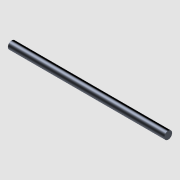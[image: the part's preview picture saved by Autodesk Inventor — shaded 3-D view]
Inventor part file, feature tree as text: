
AUTODESK INVENTOR PART (.ipt)
format: ipt  version: 2021 (Build 250183000, 183)  size: 96,768 bytes
history: native  units: in
note: dims shown in document units (in); Inventor stores cm internally (conversion verified against a paired STEP export)
features: other x1, extrude x1, imported_body x1
ambient origin geometry x8: Origin, YZ Plane, XZ Plane, XY Plane, X Axis, Y Axis, Z Axis, Center Point
bodies: Body1 (feature_tree)
feature tree (3):
  other  "Pin"
  extrude  "Extrude1"  [1 undecoded]
  imported_body  "Base1"
note: 1 required parameter value undecoded (feature->parameter linkage not recoverable at this tier; creation-order binding heuristic only, values carry confidence <= 0.55)
